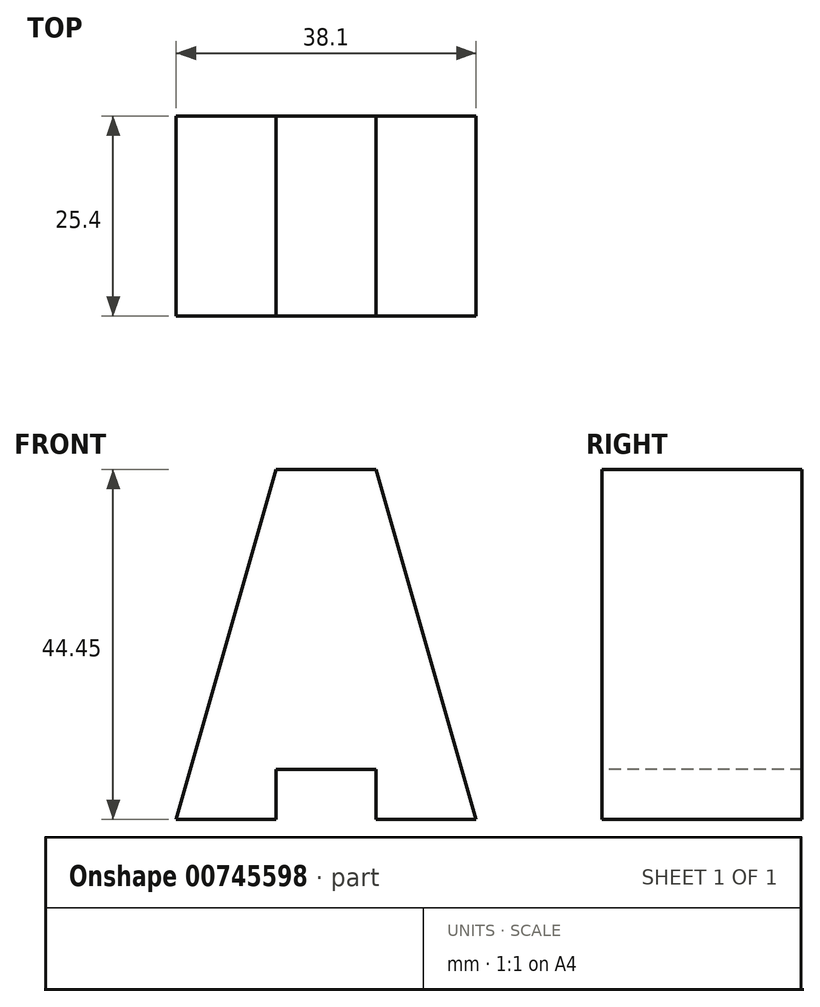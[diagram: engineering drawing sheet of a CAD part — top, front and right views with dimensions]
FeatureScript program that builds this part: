
annotation { "Feature Type Name" : "Feature", "Feature Type Description" : "" }
export const myFeature = defineFeature(function(context is Context, id is Id, definition is map)
    precondition{}
    {
        {
            var Q0;
            Q0=qCreatedBy(makeId("Front.planeOp"),FACE);
            var sketch = newSketch(context, id + "F0", { "sketchPlane" : qUnion([Q0])});
            skLineSegment(sketch, "E0", {"start": v(0, 0) * mm, "end": v(38.1, 0) * mm});
            skLineSegment(sketch, "E1", {"start": v(38.1, 0) * mm, "end": v(38.1, 44.45) * mm});
            skLineSegment(sketch, "E2", {"start": v(38.1, 44.45) * mm, "end": v(0, 44.45) * mm});
            skLineSegment(sketch, "E3", {"start": v(0, 44.45) * mm, "end": v(0, 0) * mm});
            skSolve(sketch);
        }
        {
            var Q0;
            Q0 = qSketchRegion(id + "F0", true);
            extrude(context, id + "F1", {"entities" : qUnion([Q0]), "depth" : 25.4 * mm, "offsetDistance" : 25.4 * mm});
        }
        {
            var Q0;
            Q0=makeQuery(id+"F1.opExtrude","CAP_FACE",FACE,{"disambiguationData":[OSD([sQuery(id+"F0.wireOp",EDGE,"E0"),sQuery(id+"F0.wireOp",EDGE,"E1"),sQuery(id+"F0.wireOp",EDGE,"E2"),sQuery(id+"F0.wireOp",EDGE,"E3")])],"isStart":false});
            var sketch = newSketch(context, id + "F2", { "sketchPlane" : qUnion([Q0])});
            skLineSegment(sketch, "E4.bottom", {"start": v(12.7, 0) * mm, "end": v(25.4, 0) * mm});
            skLineSegment(sketch, "E4.top", {"start": v(12.7, 6.35) * mm, "end": v(25.4, 6.35) * mm});
            skLineSegment(sketch, "E4.left", {"start": v(12.7, 0) * mm, "end": v(12.7, 6.35) * mm});
            skLineSegment(sketch, "E4.right", {"start": v(25.4, 0) * mm, "end": v(25.4, 6.35) * mm});
            skSolve(sketch);
        }
        {
            var Q0;
            Q0=makeQuery(id+"F2.imprint","IMPRINT",FACE,{"disambiguationData":[TD([[makeQuery(id+"F2.imprint","IMPRINT",EDGE,{"derivedFrom":sQuery(id+"F2.wireOp",EDGE,"E4.bottom")}),1.0]])]});
            extrude(context, id + "F3", {"entities" : qUnion([Q0]), "operationType" : NewBodyOperationType.REMOVE, "oppositeDirection" : true, "depth" : 25.4 * mm, "offsetDistance" : 25.4 * mm});
        }
        {
            var Q0;
            Q0=makeQuery(id+"F1.opExtrude","CAP_FACE",FACE,{"disambiguationData":[OSD([sQuery(id+"F0.wireOp",EDGE,"E0"),sQuery(id+"F0.wireOp",EDGE,"E1"),sQuery(id+"F0.wireOp",EDGE,"E2"),sQuery(id+"F0.wireOp",EDGE,"E3")])],"isStart":false});
            var sketch = newSketch(context, id + "F4", { "sketchPlane" : qUnion([Q0])});
            skLineSegment(sketch, "E5", {"start": v(25.4, 44.45) * mm, "end": v(38.1, 0) * mm});
            skLineSegment(sketch, "E6", {"start": v(12.7, 44.45) * mm, "end": v(0, 0) * mm});
            skSolve(sketch);
        }
        {
            var Q0;
            {var subQ0=sQuery(id+"F4.wireOp",EDGE,"E5");Q0=makeQuery(id+"F4.imprint","IMPRINT",FACE,{"disambiguationData":[TD([[makeQuery(id+"F4.imprint","IMPRINT",EDGE,{"derivedFrom":subQ0}),1.0]])]});}
            extrude(context, id + "F5", {"entities" : qUnion([Q0]), "operationType" : NewBodyOperationType.REMOVE, "oppositeDirection" : true, "depth" : 25.4 * mm, "offsetDistance" : 25.4 * mm});
        }
        {
            var Q0;
            {var subQ0=sQuery(id+"F4.wireOp",EDGE,"E5");Q0=makeQuery(id+"F4.imprint","IMPRINT",FACE,{"disambiguationData":[TD([[makeQuery(id+"F4.imprint","IMPRINT",EDGE,{"derivedFrom":subQ0}),1.0]])]});}
            extrude(context, id + "F6", {"entities" : qUnion([Q0]), "operationType" : NewBodyOperationType.REMOVE, "oppositeDirection" : true, "depth" : 25.4 * mm, "offsetDistance" : 25.4 * mm});
        }
        {
            var Q0;
            Q0=makeQuery(id+"F1.opExtrude","CAP_FACE",FACE,{"disambiguationData":[OSD([sQuery(id+"F0.wireOp",EDGE,"E0"),sQuery(id+"F0.wireOp",EDGE,"E1"),sQuery(id+"F0.wireOp",EDGE,"E2"),sQuery(id+"F0.wireOp",EDGE,"E3")])],"isStart":false});
            var sketch = newSketch(context, id + "F7", { "sketchPlane" : qUnion([Q0])});
            skLineSegment(sketch, "E7", {"start": v(12.7, 44.45) * mm, "end": v(0, 0) * mm});
            skSolve(sketch);
        }
        {
            var Q0;
            {var subQ0=sQuery(id+"F7.wireOp",EDGE,"E7");Q0=makeQuery(id+"F7.imprint","IMPRINT",FACE,{"disambiguationData":[TD([[makeQuery(id+"F7.imprint","IMPRINT",EDGE,{"derivedFrom":subQ0}),-1.0]])]});}
            extrude(context, id + "F8", {"entities" : qUnion([Q0]), "operationType" : NewBodyOperationType.REMOVE, "oppositeDirection" : true, "depth" : 25.4 * mm, "offsetDistance" : 25.4 * mm});
        }
    });
